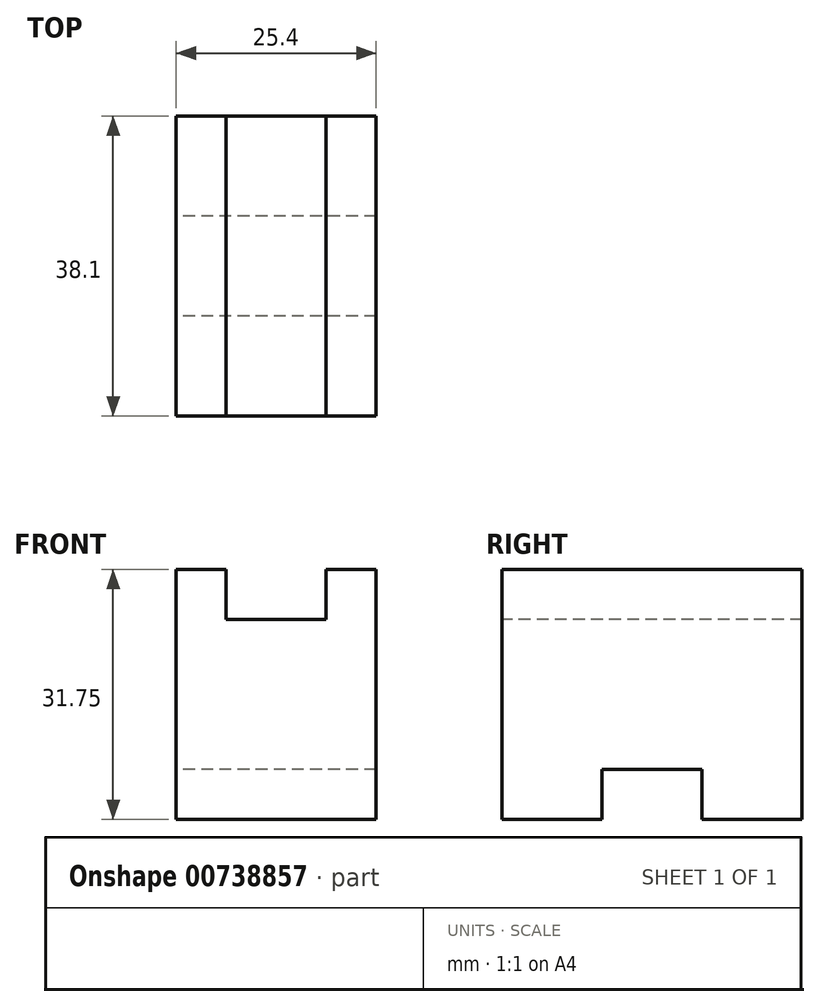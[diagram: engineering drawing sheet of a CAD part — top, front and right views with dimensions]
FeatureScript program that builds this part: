
annotation { "Feature Type Name" : "Feature", "Feature Type Description" : "" }
export const myFeature = defineFeature(function(context is Context, id is Id, definition is map)
    precondition{}
    {
        {
            var Q0;
            Q0=qCreatedBy(makeId("Right.planeOp"),FACE);
            var sketch = newSketch(context, id + "F0", { "sketchPlane" : qUnion([Q0])});
            skLineSegment(sketch, "E0", {"start": v(0, 31.75) * mm, "end": v(0, 0) * mm});
            skLineSegment(sketch, "E1", {"start": v(0, 0) * mm, "end": v(38.1, 0) * mm});
            skLineSegment(sketch, "E2", {"start": v(0, 31.75) * mm, "end": v(38.1, 31.75) * mm});
            skLineSegment(sketch, "E3", {"start": v(38.1, 0) * mm, "end": v(38.1, 31.75) * mm});
            skSolve(sketch);
        }
        {
            var Q0;
            Q0=makeQuery(id+"F0.imprint","IMPRINT",FACE,{"disambiguationData":[TD([[makeQuery(id+"F0.imprint","IMPRINT",EDGE,{"derivedFrom":sQuery(id+"F0.wireOp",EDGE,"E0")}),1.0]])]});
            extrude(context, id + "F1", {"entities" : qUnion([Q0]), "depth" : 25.4 * mm, "offsetDistance" : 25.4 * mm});
        }
        {
            var Q0;
            Q0=makeQuery(id+"F1.opExtrude","CAP_FACE",FACE,{"disambiguationData":[OSD([sQuery(id+"F0.wireOp",EDGE,"E0"),sQuery(id+"F0.wireOp",EDGE,"E1"),sQuery(id+"F0.wireOp",EDGE,"E2"),sQuery(id+"F0.wireOp",EDGE,"E3")])],"isStart":true});
            var sketch = newSketch(context, id + "F2", { "sketchPlane" : qUnion([Q0])});
            skLineSegment(sketch, "E4", {"start": v(-25.4, 0) * mm, "end": v(-25.4, 6.35) * mm});
            skLineSegment(sketch, "E5", {"start": v(-25.4, 6.35) * mm, "end": v(-12.7, 6.35) * mm});
            skLineSegment(sketch, "E6", {"start": v(-12.7, 6.35) * mm, "end": v(-12.7, 0) * mm});
            skPoint(sketch, "E7", {"position": v(-19.05, 0) * mm});
            skLineSegment(sketch, "E8", {"start": v(-25.4, 0) * mm, "end": v(-12.7, 0) * mm});
            skSolve(sketch);
        }
        {
            var Q0;
            Q0=makeQuery(id+"F2.imprint","IMPRINT",FACE,{"disambiguationData":[TD([[makeQuery(id+"F2.imprint","IMPRINT",EDGE,{"derivedFrom":sQuery(id+"F2.wireOp",EDGE,"E4")}),-1.0]])]});
            extrude(context, id + "F3", {"entities" : qUnion([Q0]), "operationType" : NewBodyOperationType.REMOVE, "endBound" : BoundingType.THROUGH_ALL, "oppositeDirection" : true, "depth" : 25.4 * mm, "offsetDistance" : 25.4 * mm});
        }
        {
            var Q0;
            Q0=makeQuery(id+"F1.opExtrude","SWEPT_FACE",FACE,{"disambiguationData":[OSD([sQuery(id+"F0.wireOp",EDGE,"E3")])]});
            var sketch = newSketch(context, id + "F4", { "sketchPlane" : qUnion([Q0])});
            skLineSegment(sketch, "E9", {"start": v(-19.05, 31.75) * mm, "end": v(-19.05, 25.4) * mm});
            skLineSegment(sketch, "E10", {"start": v(-19.05, 25.4) * mm, "end": v(-6.35, 25.4) * mm});
            skLineSegment(sketch, "E11", {"start": v(-6.35, 25.4) * mm, "end": v(-6.35, 31.75) * mm});
            skLineSegment(sketch, "E12", {"start": v(-6.35, 31.72) * mm, "end": v(-19.05, 31.75) * mm});
            skSolve(sketch);
        }
        {
            var Q0;
            Q0=makeQuery(id+"F1.opExtrude","SWEPT_FACE",FACE,{"disambiguationData":[OSD([sQuery(id+"F0.wireOp",EDGE,"E2")])]});
            var sketch = newSketch(context, id + "F5", { "sketchPlane" : qUnion([Q0])});
            skSolve(sketch);
        }
        {
            var Q0;
            {var subQ0=sQuery(id+"F0.wireOp",EDGE,"E2");Q0=makeQuery(id+"F5.imprint","IMPRINT",FACE,{"disambiguationData":[TD([[makeQuery(id+"F5.imprint","IMPRINT",EDGE,{"derivedFrom":makeQuery(id+"F1.opExtrude","CAP_EDGE",EDGE,{"disambiguationData":[OSD([subQ0])],"isStart":true})}),-1.0]])]});}
            var sketch = newSketch(context, id + "F6", { "sketchPlane" : qUnion([Q0])});
            skLineSegment(sketch, "E13", {"start": v(6.35, 38.1) * mm, "end": v(6.35, 0) * mm});
            skLineSegment(sketch, "E14", {"start": v(19.05, 38.1) * mm, "end": v(19.05, 0) * mm});
            skSolve(sketch);
        }
        {
            var Q0;
            Q0 = qSketchRegion(id + "F6", true);
            var Q1;
            {var subQ0=sQuery(id+"F6.wireOp",EDGE,"E13");Q1=makeQuery(id+"F6.imprint","IMPRINT",FACE,{"disambiguationData":[TD([[makeQuery(id+"F6.imprint","IMPRINT",EDGE,{"derivedFrom":subQ0}),1.0]])]});}
            extrude(context, id + "F7", {"entities" : qUnion([Q0, Q1]), "operationType" : NewBodyOperationType.REMOVE, "oppositeDirection" : true, "depth" : 6.35 * mm, "offsetDistance" : 25.4 * mm});
        }
    });
